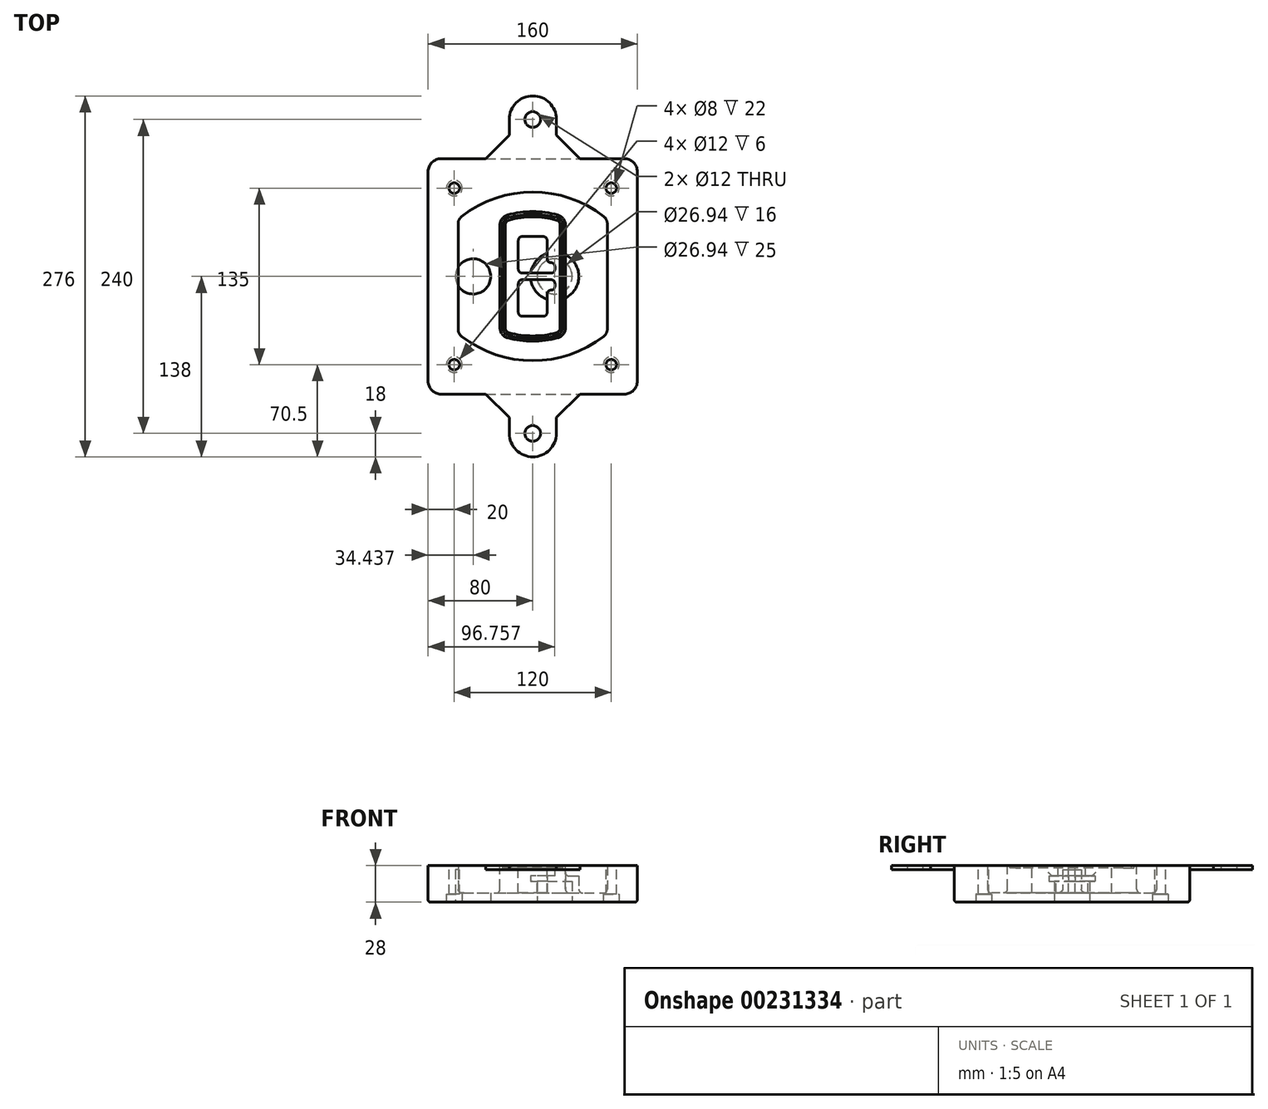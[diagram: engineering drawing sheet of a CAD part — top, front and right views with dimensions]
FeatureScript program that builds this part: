
annotation { "Feature Type Name" : "Feature", "Feature Type Description" : "" }
export const myFeature = defineFeature(function(context is Context, id is Id, definition is map)
    precondition{}
    {
        {
            var Q0;
            Q0=qCreatedBy(makeId("Top.planeOp"),FACE);
            var sketch = newSketch(context, id + "F0", { "sketchPlane" : qUnion([Q0])});
            skPoint(sketch, "E0.rect.middle", {"position": v(0, 0) * mm});
            skLineSegment(sketch, "E1.bottom", {"start": v(-70, -90) * mm, "end": v(70, -90) * mm});
            skLineSegment(sketch, "E1.top", {"start": v(-70, 90) * mm, "end": v(70, 90) * mm});
            skLineSegment(sketch, "E1.left", {"start": v(-80, -80) * mm, "end": v(-80, 80) * mm});
            skLineSegment(sketch, "E1.right", {"start": v(80, -80) * mm, "end": v(80, 80) * mm});
            skLineSegment(sketch, "E2", {"start": v(-80, 90) * mm, "end": v(80, -90) * mm, "construction": true});
            skLineSegment(sketch, "E3", {"start": v(80, 90) * mm, "end": v(-80, -90) * mm, "construction": true});
            skCircle(sketch, "E4", {"center": v(-60, 67.5) * mm, "radius": 4 * mm});
            skCircle(sketch, "E5", {"center": v(60, 67.5) * mm, "radius": 4 * mm});
            skCircle(sketch, "E6", {"center": v(60, -67.5) * mm, "radius": 4 * mm});
            skCircle(sketch, "E7", {"center": v(-60, -67.5) * mm, "radius": 4 * mm});
            skLineSegment(sketch, "E8", {"start": v(-60, 67.5) * mm, "end": v(60, 67.5) * mm, "construction": true});
            skLineSegment(sketch, "E9", {"start": v(60, 67.5) * mm, "end": v(60, -67.5) * mm, "construction": true});
            skLineSegment(sketch, "E10", {"start": v(60, -67.5) * mm, "end": v(-60, -67.5) * mm, "construction": true});
            skLineSegment(sketch, "E11", {"start": v(-60, -67.5) * mm, "end": v(-60, 67.5) * mm, "construction": true});
            skLineSegment(sketch, "E12", {"start": v(-60, 40.3) * mm, "end": v(-60, -40.3) * mm});
            skLineSegment(sketch, "E13", {"start": v(60, 40.3) * mm, "end": v(60, -40.3) * mm});
            skArc(sketch, "E14", {"start": v(56.15, 48.18) * mm, "mid": v(0, 67.5) * mm, "end": v(-56.15, 48.18) * mm});
            skArc(sketch, "E15", {"start": v(-56.15, -48.18) * mm, "mid": v(0, -67.5) * mm, "end": v(56.15, -48.18) * mm});
            skLineSegment(sketch, "E16", {"start": v(-60, 0) * mm, "end": v(60, 0) * mm, "construction": true});
            skPoint(sketch, "E17.visualSharp", {"position": v(-60, -45) * mm});
            skArc(sketch, "E17.filletArc", {"start": v(-60, -40.3) * mm, "mid": v(-58.99, -44.68) * mm, "end": v(-56.15, -48.18) * mm});
            skPoint(sketch, "E18.visualSharp", {"position": v(-60, 45) * mm});
            skArc(sketch, "E18.filletArc", {"start": v(-56.15, 48.18) * mm, "mid": v(-58.99, 44.68) * mm, "end": v(-60, 40.3) * mm});
            skPoint(sketch, "E19.visualSharp", {"position": v(60, 45) * mm});
            skArc(sketch, "E19.filletArc", {"start": v(60, 40.3) * mm, "mid": v(58.99, 44.68) * mm, "end": v(56.15, 48.18) * mm});
            skPoint(sketch, "E20.visualSharp", {"position": v(60, -45) * mm});
            skArc(sketch, "E20.filletArc", {"start": v(56.15, -48.18) * mm, "mid": v(58.99, -44.68) * mm, "end": v(60, -40.3) * mm});
            skPoint(sketch, "E21.visualSharp", {"position": v(-80, 90) * mm});
            skArc(sketch, "E21.filletArc", {"start": v(-70, 90) * mm, "mid": v(-77.07, 87.07) * mm, "end": v(-80, 80) * mm});
            skPoint(sketch, "E22.visualSharp", {"position": v(80, 90) * mm});
            skArc(sketch, "E22.filletArc", {"start": v(80, 80) * mm, "mid": v(77.07, 87.07) * mm, "end": v(70, 90) * mm});
            skPoint(sketch, "E23.visualSharp", {"position": v(80, -90) * mm});
            skArc(sketch, "E23.filletArc", {"start": v(70, -90) * mm, "mid": v(77.07, -87.07) * mm, "end": v(80, -80) * mm});
            skPoint(sketch, "E24.visualSharp", {"position": v(-80, -90) * mm});
            skArc(sketch, "E24.filletArc", {"start": v(-80, -80) * mm, "mid": v(-77.07, -87.07) * mm, "end": v(-70, -90) * mm});
            skArc(sketch, "E25.0", {"start": v(57, 40.3) * mm, "mid": v(56.3, 43.36) * mm, "end": v(54.3, 45.81) * mm});
            skLineSegment(sketch, "E25.1", {"start": v(57, 40.3) * mm, "end": v(57, -40.3) * mm});
            skArc(sketch, "E25.2", {"start": v(54.3, -45.81) * mm, "mid": v(56.3, -43.36) * mm, "end": v(57, -40.3) * mm});
            skArc(sketch, "E25.3", {"start": v(-54.3, -45.81) * mm, "mid": v(0, -64.5) * mm, "end": v(54.3, -45.81) * mm});
            skArc(sketch, "E25.4", {"start": v(-57, -40.3) * mm, "mid": v(-56.3, -43.36) * mm, "end": v(-54.3, -45.81) * mm});
            skArc(sketch, "E25.5", {"start": v(54.3, 45.81) * mm, "mid": v(0, 64.5) * mm, "end": v(-54.3, 45.81) * mm});
            skLineSegment(sketch, "E25.6", {"start": v(-57, 40.3) * mm, "end": v(-57, -40.3) * mm});
            skArc(sketch, "E25.7", {"start": v(-54.3, 45.81) * mm, "mid": v(-56.3, 43.36) * mm, "end": v(-57, 40.3) * mm});
            skArc(sketch, "E26.0", {"start": v(-58.62, 51.33) * mm, "mid": v(-62.58, 46.43) * mm, "end": v(-64, 40.3) * mm});
            skArc(sketch, "E26.1", {"start": v(58.62, 51.33) * mm, "mid": v(0, 71.5) * mm, "end": v(-58.62, 51.33) * mm});
            skArc(sketch, "E26.2", {"start": v(64, 40.3) * mm, "mid": v(62.58, 46.43) * mm, "end": v(58.62, 51.33) * mm});
            skLineSegment(sketch, "E26.3", {"start": v(64, 40.3) * mm, "end": v(64, -40.3) * mm});
            skArc(sketch, "E26.4", {"start": v(58.62, -51.33) * mm, "mid": v(62.58, -46.43) * mm, "end": v(64, -40.3) * mm});
            skLineSegment(sketch, "E26.5", {"start": v(-64, 40.3) * mm, "end": v(-64, -40.3) * mm});
            skArc(sketch, "E26.6", {"start": v(-58.62, -51.33) * mm, "mid": v(0, -71.5) * mm, "end": v(58.62, -51.33) * mm});
            skArc(sketch, "E26.7", {"start": v(-64, -40.3) * mm, "mid": v(-62.58, -46.43) * mm, "end": v(-58.62, -51.33) * mm});
            skSolve(sketch);
        }
        {
            var Q0;
            Q0=makeQuery(id+"F0.imprint","IMPRINT",FACE,{"disambiguationData":[TD([[makeQuery(id+"F0.imprint","IMPRINT",EDGE,{"derivedFrom":sQuery(id+"F0.wireOp",EDGE,"E1.bottom")}),1.0]])]});
            var Q1;
            Q1=makeQuery(id+"F0.imprint","IMPRINT",FACE,{"disambiguationData":[TD([[makeQuery(id+"F0.imprint","IMPRINT",EDGE,{"derivedFrom":sQuery(id+"F0.wireOp",EDGE,"E12")}),1.0]])]});
            var Q2;
            Q2=makeQuery(id+"F0.imprint","IMPRINT",FACE,{"disambiguationData":[TD([[makeQuery(id+"F0.imprint","IMPRINT",EDGE,{"derivedFrom":sQuery(id+"F0.wireOp",EDGE,"E25.0")}),1.0]])]});
            var Q3;
            Q3=makeQuery(id+"F0.imprint","IMPRINT",FACE,{"disambiguationData":[TD([[makeQuery(id+"F0.imprint","IMPRINT",EDGE,{"derivedFrom":sQuery(id+"F0.wireOp",EDGE,"E12")}),-1.0]])]});
            extrude(context, id + "F1", {"entities" : qUnion([Q0, Q1, Q2, Q3]), "oppositeDirection" : true, "depth" : 25 * mm});
        }
        {
            var Q0;
            Q0=makeQuery(id+"F0.imprint","IMPRINT",FACE,{"disambiguationData":[TD([[makeQuery(id+"F0.imprint","IMPRINT",EDGE,{"derivedFrom":sQuery(id+"F0.wireOp",EDGE,"E12")}),1.0]])]});
            extrude(context, id + "F2", {"entities" : qUnion([Q0]), "operationType" : NewBodyOperationType.ADD, "depth" : 3 * mm});
        }
        {
            var Q0;
            Q0=makeQuery(id+"F0.imprint","IMPRINT",FACE,{"disambiguationData":[TD([[makeQuery(id+"F0.imprint","IMPRINT",EDGE,{"derivedFrom":sQuery(id+"F0.wireOp",EDGE,"E25.0")}),1.0]])]});
            extrude(context, id + "F3", {"entities" : qUnion([Q0]), "operationType" : NewBodyOperationType.REMOVE, "oppositeDirection" : true, "depth" : 18 * mm});
        }
        {
            var Q0;
            Q0=makeQuery(id+"F2.opExtrude","CAP_FACE",FACE,{"disambiguationData":[OSD([sQuery(id+"F0.wireOp",EDGE,"E12"),sQuery(id+"F0.wireOp",EDGE,"E13"),sQuery(id+"F0.wireOp",EDGE,"E14"),sQuery(id+"F0.wireOp",EDGE,"E15"),sQuery(id+"F0.wireOp",EDGE,"E17.filletArc"),sQuery(id+"F0.wireOp",EDGE,"E18.filletArc"),sQuery(id+"F0.wireOp",EDGE,"E19.filletArc"),sQuery(id+"F0.wireOp",EDGE,"E20.filletArc"),sQuery(id+"F0.wireOp",EDGE,"E25.0"),sQuery(id+"F0.wireOp",EDGE,"E25.1"),sQuery(id+"F0.wireOp",EDGE,"E25.2"),sQuery(id+"F0.wireOp",EDGE,"E25.3"),sQuery(id+"F0.wireOp",EDGE,"E25.4"),sQuery(id+"F0.wireOp",EDGE,"E25.5"),sQuery(id+"F0.wireOp",EDGE,"E25.6"),sQuery(id+"F0.wireOp",EDGE,"E25.7")])],"isStart":false});
            var sketch = newSketch(context, id + "F4", { "sketchPlane" : qUnion([Q0])});
            skArc(sketch, "E27.0", {"start": v(-19.08, -46.97) * mm, "mid": v(0, -49.5) * mm, "end": v(19.08, -46.97) * mm});
            skArc(sketch, "E28.0", {"start": v(19.08, 46.97) * mm, "mid": v(0, 49.5) * mm, "end": v(-19.08, 46.97) * mm});
            skLineSegment(sketch, "E29", {"start": v(-25, 39.25) * mm, "end": v(-25, -39.25) * mm});
            skLineSegment(sketch, "E30", {"start": v(25, 39.25) * mm, "end": v(25, -39.25) * mm});
            skLineSegment(sketch, "E31", {"start": v(-25, 45.1) * mm, "end": v(25, 45.1) * mm, "construction": true});
            skLineSegment(sketch, "E32", {"start": v(-25, -45.1) * mm, "end": v(25, -45.1) * mm, "construction": true});
            skPoint(sketch, "E33.visualSharp", {"position": v(-25, 45.1) * mm});
            skArc(sketch, "E33.filletArc", {"start": v(-19.08, 46.97) * mm, "mid": v(-23.35, 44.11) * mm, "end": v(-25, 39.25) * mm});
            skPoint(sketch, "E34.visualSharp", {"position": v(25, 45.1) * mm});
            skArc(sketch, "E34.filletArc", {"start": v(25, 39.25) * mm, "mid": v(23.35, 44.11) * mm, "end": v(19.08, 46.97) * mm});
            skPoint(sketch, "E35.visualSharp", {"position": v(25, -45.1) * mm});
            skArc(sketch, "E35.filletArc", {"start": v(19.08, -46.97) * mm, "mid": v(23.35, -44.11) * mm, "end": v(25, -39.25) * mm});
            skPoint(sketch, "E36.visualSharp", {"position": v(-25, -45.1) * mm});
            skArc(sketch, "E36.filletArc", {"start": v(-25, -39.25) * mm, "mid": v(-23.35, -44.11) * mm, "end": v(-19.08, -46.97) * mm});
            skArc(sketch, "E37.0", {"start": v(54.3, 45.81) * mm, "mid": v(0, 64.5) * mm, "end": v(-54.3, 45.81) * mm});
            skArc(sketch, "E37.1", {"start": v(-54.3, 45.81) * mm, "mid": v(-56.3, 43.36) * mm, "end": v(-57, 40.3) * mm});
            skLineSegment(sketch, "E37.2", {"start": v(-57, 40.3) * mm, "end": v(-57, -40.3) * mm});
            skArc(sketch, "E37.3", {"start": v(-57, -40.3) * mm, "mid": v(-56.3, -43.36) * mm, "end": v(-54.3, -45.81) * mm});
            skArc(sketch, "E37.4", {"start": v(-54.3, -45.81) * mm, "mid": v(0, -64.5) * mm, "end": v(54.3, -45.81) * mm});
            skArc(sketch, "E37.5", {"start": v(54.3, -45.81) * mm, "mid": v(56.3, -43.36) * mm, "end": v(57, -40.3) * mm});
            skLineSegment(sketch, "E37.6", {"start": v(57, 40.3) * mm, "end": v(57, -40.3) * mm});
            skArc(sketch, "E37.7", {"start": v(57, 40.3) * mm, "mid": v(56.3, 43.36) * mm, "end": v(54.3, 45.81) * mm});
            skLineSegment(sketch, "E38.0", {"start": v(23, 39.25) * mm, "end": v(23, -39.25) * mm});
            skArc(sketch, "E38.1", {"start": v(18.56, -45.04) * mm, "mid": v(21.76, -42.9) * mm, "end": v(23, -39.25) * mm});
            skArc(sketch, "E38.2", {"start": v(-18.56, -45.04) * mm, "mid": v(0, -47.5) * mm, "end": v(18.56, -45.04) * mm});
            skArc(sketch, "E38.3", {"start": v(-23, -39.25) * mm, "mid": v(-21.76, -42.9) * mm, "end": v(-18.56, -45.04) * mm});
            skLineSegment(sketch, "E38.4", {"start": v(-23, 39.25) * mm, "end": v(-23, -39.25) * mm});
            skArc(sketch, "E38.5", {"start": v(23, 39.25) * mm, "mid": v(21.76, 42.9) * mm, "end": v(18.56, 45.04) * mm});
            skArc(sketch, "E38.6", {"start": v(-18.56, 45.04) * mm, "mid": v(-21.76, 42.9) * mm, "end": v(-23, 39.25) * mm});
            skArc(sketch, "E38.7", {"start": v(18.56, 45.04) * mm, "mid": v(0, 47.5) * mm, "end": v(-18.56, 45.04) * mm});
            skArc(sketch, "E39.0", {"start": v(21, 39.25) * mm, "mid": v(20.18, 41.68) * mm, "end": v(18.04, 43.1) * mm});
            skLineSegment(sketch, "E39.1", {"start": v(21, 39.25) * mm, "end": v(21, -39.25) * mm});
            skArc(sketch, "E39.2", {"start": v(18.04, -43.1) * mm, "mid": v(20.18, -41.68) * mm, "end": v(21, -39.25) * mm});
            skArc(sketch, "E39.3", {"start": v(-18.04, -43.1) * mm, "mid": v(0, -45.5) * mm, "end": v(18.04, -43.1) * mm});
            skArc(sketch, "E39.4", {"start": v(-21, -39.25) * mm, "mid": v(-20.18, -41.68) * mm, "end": v(-18.04, -43.1) * mm});
            skArc(sketch, "E39.5", {"start": v(18.04, 43.1) * mm, "mid": v(0, 45.5) * mm, "end": v(-18.04, 43.1) * mm});
            skLineSegment(sketch, "E39.6", {"start": v(-21, 39.25) * mm, "end": v(-21, -39.25) * mm});
            skArc(sketch, "E39.7", {"start": v(-18.04, 43.1) * mm, "mid": v(-20.18, 41.68) * mm, "end": v(-21, 39.25) * mm});
            skLineSegment(sketch, "E40", {"start": v(-25, 0) * mm, "end": v(25, 0) * mm, "construction": true});
            skLineSegment(sketch, "E41", {"start": v(-11, 5.5) * mm, "end": v(-11, 27.5) * mm});
            skLineSegment(sketch, "E42", {"start": v(-8, 30.5) * mm, "end": v(8, 30.5) * mm});
            skLineSegment(sketch, "E43", {"start": v(11, 27.5) * mm, "end": v(11, 13.5) * mm});
            skLineSegment(sketch, "E44", {"start": v(14, 10.5) * mm, "end": v(14, 10.5) * mm});
            skLineSegment(sketch, "E45", {"start": v(17, 7.5) * mm, "end": v(17, 5.5) * mm});
            skLineSegment(sketch, "E46", {"start": v(14, 2.5) * mm, "end": v(-8, 2.5) * mm});
            skPoint(sketch, "E47.visualSharp", {"position": v(-11, 30.5) * mm});
            skArc(sketch, "E47.filletArc", {"start": v(-8, 30.5) * mm, "mid": v(-10.12, 29.62) * mm, "end": v(-11, 27.5) * mm});
            skPoint(sketch, "E48.visualSharp", {"position": v(11, 30.5) * mm});
            skArc(sketch, "E48.filletArc", {"start": v(11, 27.5) * mm, "mid": v(10.12, 29.62) * mm, "end": v(8, 30.5) * mm});
            skPoint(sketch, "E49.visualSharp", {"position": v(11, 10.5) * mm});
            skArc(sketch, "E49.filletArc", {"start": v(11, 13.5) * mm, "mid": v(11.88, 11.38) * mm, "end": v(14, 10.5) * mm});
            skPoint(sketch, "E50.visualSharp", {"position": v(17, 10.5) * mm});
            skArc(sketch, "E50.filletArc", {"start": v(17, 7.5) * mm, "mid": v(16.12, 9.62) * mm, "end": v(14, 10.5) * mm});
            skPoint(sketch, "E51.visualSharp", {"position": v(17, 2.5) * mm});
            skArc(sketch, "E51.filletArc", {"start": v(14, 2.5) * mm, "mid": v(16.12, 3.38) * mm, "end": v(17, 5.5) * mm});
            skPoint(sketch, "E52.visualSharp", {"position": v(-11, 2.5) * mm});
            skArc(sketch, "E52.filletArc", {"start": v(-11, 5.5) * mm, "mid": v(-10.12, 3.38) * mm, "end": v(-8, 2.5) * mm});
            skLineSegment(sketch, "E53.0.MirrorCS", {"start": v(14, -2.5) * mm, "end": v(-8, -2.5) * mm});
            skArc(sketch, "E54.0.MirrorCS", {"start": v(-11, -5.5) * mm, "mid": v(-10.12, -3.38) * mm, "end": v(-8, -2.5) * mm});
            skLineSegment(sketch, "E55.0.MirrorCS", {"start": v(-11, -5.5) * mm, "end": v(-11, -27.5) * mm});
            skArc(sketch, "E56.0.MirrorCS", {"start": v(-8, -30.5) * mm, "mid": v(-10.12, -29.62) * mm, "end": v(-11, -27.5) * mm});
            skLineSegment(sketch, "E57.0.MirrorCS", {"start": v(-8, -30.5) * mm, "end": v(8, -30.5) * mm});
            skArc(sketch, "E58.0.MirrorCS", {"start": v(11, -27.5) * mm, "mid": v(10.12, -29.62) * mm, "end": v(8, -30.5) * mm});
            skLineSegment(sketch, "E59.0.MirrorCS", {"start": v(11, -27.5) * mm, "end": v(11, -13.5) * mm});
            skArc(sketch, "E60.0.MirrorCS", {"start": v(11, -13.5) * mm, "mid": v(11.88, -11.38) * mm, "end": v(14, -10.5) * mm});
            skArc(sketch, "E61.0.MirrorCS", {"start": v(17, -7.5) * mm, "mid": v(16.12, -9.62) * mm, "end": v(14, -10.5) * mm});
            skLineSegment(sketch, "E62.0.MirrorCS", {"start": v(17, -7.5) * mm, "end": v(17, -5.5) * mm});
            skArc(sketch, "E63.0.MirrorCS", {"start": v(14, -2.5) * mm, "mid": v(16.12, -3.38) * mm, "end": v(17, -5.5) * mm});
            skSolve(sketch);
        }
        {
            var Q0;
            Q0=makeQuery(id+"F4.imprint","IMPRINT",FACE,{"disambiguationData":[TD([[makeQuery(id+"F4.imprint","IMPRINT",EDGE,{"derivedFrom":sQuery(id+"F4.wireOp",EDGE,"E27.0")}),1.0]])]});
            var Q1;
            Q1=makeQuery(id+"F4.imprint","IMPRINT",FACE,{"disambiguationData":[TD([[makeQuery(id+"F4.imprint","IMPRINT",EDGE,{"derivedFrom":sQuery(id+"F4.wireOp",EDGE,"E38.0")}),-1.0]])]});
            var Q2;
            Q2=makeQuery(id+"F4.imprint","IMPRINT",FACE,{"disambiguationData":[TD([[makeQuery(id+"F4.imprint","IMPRINT",EDGE,{"derivedFrom":sQuery(id+"F4.wireOp",EDGE,"E39.0")}),1.0]])]});
            extrude(context, id + "F5", {"entities" : qUnion([Q0, Q1, Q2]), "operationType" : NewBodyOperationType.ADD, "endBound" : BoundingType.UP_TO_NEXT, "oppositeDirection" : true, "depth" : 25 * mm});
        }
        {
            var Q0;
            Q0=makeQuery(id+"F4.imprint","IMPRINT",FACE,{"disambiguationData":[TD([[makeQuery(id+"F4.imprint","IMPRINT",EDGE,{"derivedFrom":sQuery(id+"F4.wireOp",EDGE,"E38.0")}),-1.0]])]});
            extrude(context, id + "F6", {"entities" : qUnion([Q0]), "operationType" : NewBodyOperationType.REMOVE, "oppositeDirection" : true, "depth" : 2 * mm});
        }
        {
            var Q0;
            Q0=makeQuery(id+"F1.opExtrude","CAP_FACE",FACE,{"disambiguationData":[OSD([sQuery(id+"F0.wireOp",EDGE,"E1.bottom"),sQuery(id+"F0.wireOp",EDGE,"E1.top"),sQuery(id+"F0.wireOp",EDGE,"E1.left"),sQuery(id+"F0.wireOp",EDGE,"E1.right"),sQuery(id+"F0.wireOp",EDGE,"E4"),sQuery(id+"F0.wireOp",EDGE,"E5"),sQuery(id+"F0.wireOp",EDGE,"E6"),sQuery(id+"F0.wireOp",EDGE,"E7"),sQuery(id+"F0.wireOp",EDGE,"E21.filletArc"),sQuery(id+"F0.wireOp",EDGE,"E22.filletArc"),sQuery(id+"F0.wireOp",EDGE,"E23.filletArc"),sQuery(id+"F0.wireOp",EDGE,"E24.filletArc")])],"isStart":false});
            var sketch = newSketch(context, id + "F7", { "sketchPlane" : qUnion([Q0])});
            skCircle(sketch, "E64", {"center": v(16.76, 0) * mm, "radius": 13.47 * mm});
            skCircle(sketch, "E65", {"center": v(-45.56, 0) * mm, "radius": 13.47 * mm});
            skLineSegment(sketch, "E66", {"start": v(80, 0) * mm, "end": v(-80, 0) * mm});
            skCircle(sketch, "E67", {"center": v(16.76, 0) * mm, "radius": 18.47 * mm});
            skCircle(sketch, "E68", {"center": v(60, -67.5) * mm, "radius": 6 * mm});
            skCircle(sketch, "E69", {"center": v(-60, -67.5) * mm, "radius": 6 * mm});
            skCircle(sketch, "E70", {"center": v(-60, 67.5) * mm, "radius": 6 * mm});
            skCircle(sketch, "E71", {"center": v(60, 67.5) * mm, "radius": 6 * mm});
            skSolve(sketch);
        }
        {
            var Q0;
            {var subQ1=sQuery(id+"F7.wireOp",EDGE,"E66");var subQ4=sQuery(id+"F7.wireOp",EDGE,"E64");var subQ6=makeQuery(id+"F7.imprint","INTERSECT",VERTEX,{"disambiguationData":[OD(0.0)],"derivedFrom":[subQ4,subQ1]});Q0=makeQuery(id+"F7.imprint","IMPRINT",FACE,{"disambiguationData":[TD([[makeQuery(id+"F7.imprint","IMPRINT",EDGE,{"disambiguationData":[TD([[subQ6,-1.0]])],"derivedFrom":subQ4}),-1.0]])]});}
            var Q1;
            {var subQ0=sQuery(id+"F7.wireOp",EDGE,"E66");var subQ1=sQuery(id+"F7.wireOp",EDGE,"E64");var subQ3=makeQuery(id+"F7.imprint","INTERSECT",VERTEX,{"disambiguationData":[OD(0.0)],"derivedFrom":[subQ1,subQ0]});Q1=makeQuery(id+"F7.imprint","IMPRINT",FACE,{"disambiguationData":[TD([[makeQuery(id+"F7.imprint","IMPRINT",EDGE,{"disambiguationData":[TD([[subQ3,-1.0]])],"derivedFrom":subQ1}),1.0]])]});}
            var Q2;
            {var subQ0=sQuery(id+"F7.wireOp",EDGE,"E66");var subQ1=sQuery(id+"F7.wireOp",EDGE,"E64");var subQ3=makeQuery(id+"F7.imprint","INTERSECT",VERTEX,{"disambiguationData":[OD(0.0)],"derivedFrom":[subQ1,subQ0]});Q2=makeQuery(id+"F7.imprint","IMPRINT",FACE,{"disambiguationData":[TD([[makeQuery(id+"F7.imprint","IMPRINT",EDGE,{"disambiguationData":[TD([[subQ3,1.0]])],"derivedFrom":subQ1}),1.0]])]});}
            var Q3;
            {var subQ1=sQuery(id+"F7.wireOp",EDGE,"E66");var subQ4=sQuery(id+"F7.wireOp",EDGE,"E64");var subQ6=makeQuery(id+"F7.imprint","INTERSECT",VERTEX,{"disambiguationData":[OD(0.0)],"derivedFrom":[subQ4,subQ1]});Q3=makeQuery(id+"F7.imprint","IMPRINT",FACE,{"disambiguationData":[TD([[makeQuery(id+"F7.imprint","IMPRINT",EDGE,{"disambiguationData":[TD([[subQ6,1.0]])],"derivedFrom":subQ4}),-1.0]])]});}
            extrude(context, id + "F8", {"entities" : qUnion([Q0, Q1, Q2, Q3]), "operationType" : NewBodyOperationType.ADD, "oppositeDirection" : true, "depth" : 20 * mm});
        }
        {
            var Q0;
            {var subQ0=sQuery(id+"F7.wireOp",EDGE,"E66");var subQ1=sQuery(id+"F7.wireOp",EDGE,"E64");var subQ3=makeQuery(id+"F7.imprint","INTERSECT",VERTEX,{"disambiguationData":[OD(0.0)],"derivedFrom":[subQ1,subQ0]});Q0=makeQuery(id+"F7.imprint","IMPRINT",FACE,{"disambiguationData":[TD([[makeQuery(id+"F7.imprint","IMPRINT",EDGE,{"disambiguationData":[TD([[subQ3,-1.0]])],"derivedFrom":subQ1}),1.0]])]});}
            var Q1;
            {var subQ0=sQuery(id+"F7.wireOp",EDGE,"E66");var subQ1=sQuery(id+"F7.wireOp",EDGE,"E64");var subQ3=makeQuery(id+"F7.imprint","INTERSECT",VERTEX,{"disambiguationData":[OD(0.0)],"derivedFrom":[subQ1,subQ0]});Q1=makeQuery(id+"F7.imprint","IMPRINT",FACE,{"disambiguationData":[TD([[makeQuery(id+"F7.imprint","IMPRINT",EDGE,{"disambiguationData":[TD([[subQ3,1.0]])],"derivedFrom":subQ1}),1.0]])]});}
            extrude(context, id + "F9", {"entities" : qUnion([Q0, Q1]), "operationType" : NewBodyOperationType.REMOVE, "oppositeDirection" : true, "depth" : 16 * mm});
        }
        {
            var Q0;
            {var subQ0=sQuery(id+"F7.wireOp",EDGE,"E66");var subQ1=sQuery(id+"F7.wireOp",EDGE,"E65");var subQ3=makeQuery(id+"F7.imprint","INTERSECT",VERTEX,{"disambiguationData":[OD(0.0)],"derivedFrom":[subQ1,subQ0]});Q0=makeQuery(id+"F7.imprint","IMPRINT",FACE,{"disambiguationData":[TD([[makeQuery(id+"F7.imprint","IMPRINT",EDGE,{"disambiguationData":[TD([[subQ3,-1.0]])],"derivedFrom":subQ1}),1.0]])]});}
            var Q1;
            {var subQ0=sQuery(id+"F7.wireOp",EDGE,"E66");var subQ1=sQuery(id+"F7.wireOp",EDGE,"E65");var subQ3=makeQuery(id+"F7.imprint","INTERSECT",VERTEX,{"disambiguationData":[OD(0.0)],"derivedFrom":[subQ1,subQ0]});Q1=makeQuery(id+"F7.imprint","IMPRINT",FACE,{"disambiguationData":[TD([[makeQuery(id+"F7.imprint","IMPRINT",EDGE,{"disambiguationData":[TD([[subQ3,1.0]])],"derivedFrom":subQ1}),1.0]])]});}
            extrude(context, id + "F10", {"entities" : qUnion([Q0, Q1]), "operationType" : NewBodyOperationType.REMOVE, "oppositeDirection" : true, "depth" : 25 * mm});
        }
        {
            var Q0;
            Q0=makeQuery(id+"F7.imprint","IMPRINT",FACE,{"disambiguationData":[TD([[makeQuery(id+"F7.imprint","IMPRINT",EDGE,{"derivedFrom":sQuery(id+"F7.wireOp",EDGE,"E68")}),1.0]])]});
            var Q1;
            Q1=makeQuery(id+"F7.imprint","IMPRINT",FACE,{"disambiguationData":[TD([[makeQuery(id+"F7.imprint","IMPRINT",EDGE,{"derivedFrom":makeQuery(id+"F1.opExtrude","CAP_EDGE",EDGE,{"disambiguationData":[OSD([sQuery(id+"F0.wireOp",EDGE,"E5")])],"isStart":false})}),-1.0]])]});
            var Q2;
            Q2=makeQuery(id+"F7.imprint","IMPRINT",FACE,{"disambiguationData":[TD([[makeQuery(id+"F7.imprint","IMPRINT",EDGE,{"derivedFrom":sQuery(id+"F7.wireOp",EDGE,"E69")}),1.0]])]});
            var Q3;
            Q3=makeQuery(id+"F7.imprint","IMPRINT",FACE,{"disambiguationData":[TD([[makeQuery(id+"F7.imprint","IMPRINT",EDGE,{"derivedFrom":makeQuery(id+"F1.opExtrude","CAP_EDGE",EDGE,{"disambiguationData":[OSD([sQuery(id+"F0.wireOp",EDGE,"E4")])],"isStart":false})}),-1.0]])]});
            var Q4;
            Q4=makeQuery(id+"F7.imprint","IMPRINT",FACE,{"disambiguationData":[TD([[makeQuery(id+"F7.imprint","IMPRINT",EDGE,{"derivedFrom":sQuery(id+"F7.wireOp",EDGE,"E70")}),1.0]])]});
            var Q5;
            Q5=makeQuery(id+"F7.imprint","IMPRINT",FACE,{"disambiguationData":[TD([[makeQuery(id+"F7.imprint","IMPRINT",EDGE,{"derivedFrom":makeQuery(id+"F1.opExtrude","CAP_EDGE",EDGE,{"disambiguationData":[OSD([sQuery(id+"F0.wireOp",EDGE,"E7")])],"isStart":false})}),-1.0]])]});
            var Q6;
            Q6=makeQuery(id+"F7.imprint","IMPRINT",FACE,{"disambiguationData":[TD([[makeQuery(id+"F7.imprint","IMPRINT",EDGE,{"derivedFrom":sQuery(id+"F7.wireOp",EDGE,"E71")}),1.0]])]});
            var Q7;
            Q7=makeQuery(id+"F7.imprint","IMPRINT",FACE,{"disambiguationData":[TD([[makeQuery(id+"F7.imprint","IMPRINT",EDGE,{"derivedFrom":makeQuery(id+"F1.opExtrude","CAP_EDGE",EDGE,{"disambiguationData":[OSD([sQuery(id+"F0.wireOp",EDGE,"E6")])],"isStart":false})}),-1.0]])]});
            extrude(context, id + "F11", {"entities" : qUnion([Q0, Q1, Q2, Q3, Q4, Q5, Q6, Q7]), "operationType" : NewBodyOperationType.REMOVE, "oppositeDirection" : true, "depth" : 6 * mm});
        }
        {
            var Q0;
            Q0=makeQuery(id+"F9.boolean.opBoolean","COPY",FACE,{"derivedFrom":makeQuery(id+"F9.opExtrude","CAP_FACE",FACE,{"disambiguationData":[OSD([sQuery(id+"F7.wireOp",EDGE,"E64")])],"isStart":false})});
            var sketch = newSketch(context, id + "F12", { "sketchPlane" : qUnion([Q0])});
            skArc(sketch, "E72.0", {"start": v(11, 17.55) * mm, "mid": v(2.57, 11.82) * mm, "end": v(-1.54, 2.5) * mm});
            skArc(sketch, "E72.1", {"start": v(-1.54, -2.5) * mm, "mid": v(2.57, -11.82) * mm, "end": v(11, -17.55) * mm});
            skLineSegment(sketch, "E73", {"start": v(-1.54, -2.5) * mm, "end": v(14, -2.5) * mm});
            skLineSegment(sketch, "E74.0", {"start": v(14, 2.5) * mm, "end": v(-1.54, 2.5) * mm});
            skArc(sketch, "E74.1", {"start": v(14, 2.5) * mm, "mid": v(16.12, 3.38) * mm, "end": v(17, 5.5) * mm});
            skLineSegment(sketch, "E74.2", {"start": v(17, 7.5) * mm, "end": v(17, 5.5) * mm});
            skArc(sketch, "E74.3", {"start": v(17, 7.5) * mm, "mid": v(16.12, 9.62) * mm, "end": v(14, 10.5) * mm});
            skArc(sketch, "E74.4", {"start": v(11, 13.5) * mm, "mid": v(11.88, 11.38) * mm, "end": v(14, 10.5) * mm});
            skLineSegment(sketch, "E74.5", {"start": v(11, 17.55) * mm, "end": v(11, 13.5) * mm});
            skLineSegment(sketch, "E74.7", {"start": v(14, -2.5) * mm, "end": v(-1.54, -2.5) * mm});
            skArc(sketch, "E74.8", {"start": v(14, -2.5) * mm, "mid": v(16.12, -3.38) * mm, "end": v(17, -5.5) * mm});
            skLineSegment(sketch, "E74.9", {"start": v(17, -7.5) * mm, "end": v(17, -5.5) * mm});
            skArc(sketch, "E74.10", {"start": v(17, -7.5) * mm, "mid": v(16.12, -9.62) * mm, "end": v(14, -10.5) * mm});
            skArc(sketch, "E74.11", {"start": v(11, -13.5) * mm, "mid": v(11.88, -11.38) * mm, "end": v(14, -10.5) * mm});
            skLineSegment(sketch, "E74.12", {"start": v(11, -17.55) * mm, "end": v(11, -13.5) * mm});
            skPoint(sketch, "E75.orphan", {"position": v(11, -27.5) * mm});
            skPoint(sketch, "E76.orphan", {"position": v(-8, -2.5) * mm});
            skPoint(sketch, "E77.orphan", {"position": v(-8, 2.5) * mm});
            skPoint(sketch, "E78.orphan", {"position": v(11, 27.5) * mm});
            skSolve(sketch);
        }
        {
            var Q0;
            {var subQ7=sQuery(id+"F12.wireOp",EDGE,"E72.0");var subQ14=sQuery(id+"F12.wireOp",EDGE,"E72.1");var subQ16=sQuery(id+"F12.wireOp",EDGE,"E74.1");var subQ18=sQuery(id+"F12.wireOp",EDGE,"E74.8");Q0=qUnion([makeQuery(id+"F12.imprint","IMPRINT",FACE,{"disambiguationData":[TD([[makeQuery(id+"F12.imprint","IMPRINT",EDGE,{"derivedFrom":subQ7}),1.0]])]}),makeQuery(id+"F12.imprint","IMPRINT",FACE,{"disambiguationData":[TD([[makeQuery(id+"F12.imprint","IMPRINT",EDGE,{"derivedFrom":subQ14}),1.0]])]}),makeQuery(id+"F12.imprint","IMPRINT",FACE,{"disambiguationData":[TD([[makeQuery(id+"F12.imprint","IMPRINT",EDGE,{"derivedFrom":subQ16}),1.0]])]}),makeQuery(id+"F12.imprint","IMPRINT",FACE,{"disambiguationData":[TD([[makeQuery(id+"F12.imprint","IMPRINT",EDGE,{"derivedFrom":subQ18}),-1.0]])]})]);}
            var Q1;
            Q1=makeQuery(id+"F5.boolean.opBoolean","SPLIT",FACE,{"disambiguationData":[TD([makeQuery(id+"F5.opExtrude","SWEPT_FACE",FACE,{"disambiguationData":[OSD([sQuery(id+"F4.wireOp",EDGE,"E41")])]})])],"derivedFrom":makeQuery(id+"F3.boolean.opBoolean","COPY",FACE,{"derivedFrom":makeQuery(id+"F3.opExtrude","CAP_FACE",FACE,{"disambiguationData":[OSD([sQuery(id+"F0.wireOp",EDGE,"E25.0"),sQuery(id+"F0.wireOp",EDGE,"E25.1"),sQuery(id+"F0.wireOp",EDGE,"E25.2"),sQuery(id+"F0.wireOp",EDGE,"E25.3"),sQuery(id+"F0.wireOp",EDGE,"E25.4"),sQuery(id+"F0.wireOp",EDGE,"E25.5"),sQuery(id+"F0.wireOp",EDGE,"E25.6"),sQuery(id+"F0.wireOp",EDGE,"E25.7")])],"isStart":false})})});
            extrude(context, id + "F13", {"entities" : qUnion([Q0]), "operationType" : NewBodyOperationType.REMOVE, "endBound" : BoundingType.UP_TO_SURFACE, "endBoundEntityFace" : qUnion([Q1]), "depth" : 25 * mm});
        }
        {
            var Q0;
            Q0=makeQuery(id+"F3.boolean.opBoolean","COPY",EDGE,{"derivedFrom":makeQuery(id+"F3.opExtrude","CAP_EDGE",EDGE,{"disambiguationData":[OSD([sQuery(id+"F0.wireOp",EDGE,"E25.6")])],"isStart":false})});
            var Q1;
            Q1=makeQuery(id+"F8.boolean.opBoolean","INTERSECT",EDGE,{"derivedFrom":[makeQuery(id+"F5.opExtrude","SWEPT_FACE",FACE,{"disambiguationData":[OSD([sQuery(id+"F4.wireOp",EDGE,"E30")])]}),makeQuery(id+"F8.opExtrude","CAP_FACE",FACE,{"disambiguationData":[OSD([sQuery(id+"F7.wireOp",EDGE,"E67")])],"isStart":false})]});
            var Q2;
            Q2=makeQuery(id+"F8.boolean.opBoolean","INTERSECT",EDGE,{"disambiguationData":[OD(1.0)],"derivedFrom":[makeQuery(id+"F5.opExtrude","SWEPT_FACE",FACE,{"disambiguationData":[OSD([sQuery(id+"F4.wireOp",EDGE,"E30")])]}),makeQuery(id+"F8.opExtrude","SWEPT_FACE",FACE,{"disambiguationData":[OSD([sQuery(id+"F7.wireOp",EDGE,"E67")])]})]});
            var Q3;
            {var subQ0=sQuery(id+"F4.wireOp",EDGE,"E30");Q3=makeQuery(id+"F8.boolean.opBoolean","SPLIT",EDGE,{"disambiguationData":[TD([makeQuery(id+"F5.opExtrude","SWEPT_FACE",FACE,{"disambiguationData":[OSD([sQuery(id+"F4.wireOp",EDGE,"E35.filletArc")])]})])],"derivedFrom":makeQuery(id+"F5.opExtrude","CAP_EDGE",EDGE,{"disambiguationData":[OSD([subQ0])],"isStart":false})});}
            var Q4;
            {var subQ0=sQuery(id+"F0.wireOp",EDGE,"E25.7");var subQ1=sQuery(id+"F0.wireOp",EDGE,"E25.1");var subQ2=sQuery(id+"F0.wireOp",EDGE,"E25.6");var subQ3=sQuery(id+"F0.wireOp",EDGE,"E25.5");var subQ4=sQuery(id+"F0.wireOp",EDGE,"E25.4");var subQ5=sQuery(id+"F0.wireOp",EDGE,"E25.0");var subQ6=sQuery(id+"F0.wireOp",EDGE,"E25.2");var subQ7=sQuery(id+"F0.wireOp",EDGE,"E25.3");Q4=makeQuery(id+"F8.boolean.opBoolean","INTERSECT",EDGE,{"derivedFrom":[makeQuery(id+"F5.boolean.opBoolean","SPLIT",FACE,{"disambiguationData":[TD([makeQuery(id+"F2.opExtrude","SWEPT_FACE",FACE,{"disambiguationData":[OSD([subQ5])]})])],"derivedFrom":makeQuery(id+"F3.boolean.opBoolean","COPY",FACE,{"derivedFrom":makeQuery(id+"F3.opExtrude","CAP_FACE",FACE,{"disambiguationData":[OSD([subQ5,subQ1,subQ6,subQ7,subQ4,subQ3,subQ2,subQ0])],"isStart":false})})}),makeQuery(id+"F8.opExtrude","SWEPT_FACE",FACE,{"disambiguationData":[OSD([sQuery(id+"F7.wireOp",EDGE,"E67")])]})]});}
            var Q5;
            Q5=makeQuery(id+"F8.boolean.opBoolean","INTERSECT",EDGE,{"disambiguationData":[OD(0.0)],"derivedFrom":[makeQuery(id+"F5.opExtrude","SWEPT_FACE",FACE,{"disambiguationData":[OSD([sQuery(id+"F4.wireOp",EDGE,"E30")])]}),makeQuery(id+"F8.opExtrude","SWEPT_FACE",FACE,{"disambiguationData":[OSD([sQuery(id+"F7.wireOp",EDGE,"E67")])]})]});
            fillet(context, id + "F14", {"entities" : qUnion([Q0, Q1, Q2, Q3, Q4, Q5]), "radius" : 3 * mm, "tangentPropagation" : true, "allowEdgeOverflow" : false});
        }
        {
            var Q0;
            Q0=makeQuery(id+"F1.opExtrude","CAP_EDGE",EDGE,{"disambiguationData":[OSD([sQuery(id+"F0.wireOp",EDGE,"E1.bottom")])],"isStart":false});
            fillet(context, id + "F15", {"entities" : qUnion([Q0]), "radius" : 2 * mm, "tangentPropagation" : true, "allowEdgeOverflow" : false});
        }
        {
            var Q0;
            {var subQ0=sQuery(id+"F0.wireOp",EDGE,"E22.filletArc");var subQ1=sQuery(id+"F0.wireOp",EDGE,"E7");var subQ2=sQuery(id+"F0.wireOp",EDGE,"E6");var subQ3=sQuery(id+"F0.wireOp",EDGE,"E5");var subQ4=sQuery(id+"F0.wireOp",EDGE,"E4");var subQ5=sQuery(id+"F0.wireOp",EDGE,"E1.bottom");var subQ6=sQuery(id+"F0.wireOp",EDGE,"E21.filletArc");var subQ7=sQuery(id+"F0.wireOp",EDGE,"E1.top");var subQ8=sQuery(id+"F0.wireOp",EDGE,"E1.left");var subQ9=sQuery(id+"F0.wireOp",EDGE,"E1.right");var subQ10=sQuery(id+"F0.wireOp",EDGE,"E23.filletArc");var subQ11=sQuery(id+"F0.wireOp",EDGE,"E24.filletArc");Q0=makeQuery(id+"F2.boolean.opBoolean","SPLIT",FACE,{"disambiguationData":[TD([makeQuery(id+"F1.opExtrude","SWEPT_FACE",FACE,{"disambiguationData":[OSD([subQ5])]})])],"derivedFrom":makeQuery(id+"F1.opExtrude","CAP_FACE",FACE,{"disambiguationData":[OSD([subQ5,subQ7,subQ8,subQ9,subQ4,subQ3,subQ2,subQ1,subQ6,subQ0,subQ10,subQ11])],"isStart":true})});}
            var sketch = newSketch(context, id + "F16", { "sketchPlane" : qUnion([Q0])});
            skLineSegment(sketch, "E79.0", {"start": v(-70, 90) * mm, "end": v(70, 90) * mm});
            skArc(sketch, "E79.1", {"start": v(80, 80) * mm, "mid": v(77.07, 87.07) * mm, "end": v(70, 90) * mm});
            skArc(sketch, "E79.2", {"start": v(-70, 90) * mm, "mid": v(-77.07, 87.07) * mm, "end": v(-80, 80) * mm});
            skLineSegment(sketch, "E79.3", {"start": v(-80, -80) * mm, "end": v(-80, 80) * mm});
            skCircle(sketch, "E79.4", {"center": v(-60, 67.5) * mm, "radius": 4 * mm});
            skCircle(sketch, "E79.5", {"center": v(-60, -67.5) * mm, "radius": 4 * mm});
            skArc(sketch, "E79.6", {"start": v(-80, -80) * mm, "mid": v(-77.07, -87.07) * mm, "end": v(-70, -90) * mm});
            skLineSegment(sketch, "E79.7", {"start": v(-70, -90) * mm, "end": v(70, -90) * mm});
            skCircle(sketch, "E79.8", {"center": v(60, -67.5) * mm, "radius": 4 * mm});
            skArc(sketch, "E79.9", {"start": v(70, -90) * mm, "mid": v(77.07, -87.07) * mm, "end": v(80, -80) * mm});
            skLineSegment(sketch, "E79.10", {"start": v(80, -80) * mm, "end": v(80, 80) * mm});
            skCircle(sketch, "E79.11", {"center": v(60, 67.5) * mm, "radius": 4 * mm});
            skArc(sketch, "E79.12", {"start": v(56.15, 48.18) * mm, "mid": v(0, 67.5) * mm, "end": v(-56.15, 48.18) * mm});
            skArc(sketch, "E79.13", {"start": v(60, 40.3) * mm, "mid": v(58.99, 44.68) * mm, "end": v(56.15, 48.18) * mm});
            skLineSegment(sketch, "E79.14", {"start": v(60, 40.3) * mm, "end": v(60, -40.3) * mm});
            skArc(sketch, "E79.15", {"start": v(-56.15, 48.18) * mm, "mid": v(-58.99, 44.68) * mm, "end": v(-60, 40.3) * mm});
            skLineSegment(sketch, "E79.16", {"start": v(-60, 40.3) * mm, "end": v(-60, -40.3) * mm});
            skArc(sketch, "E79.17", {"start": v(-60, -40.3) * mm, "mid": v(-58.99, -44.68) * mm, "end": v(-56.15, -48.18) * mm});
            skArc(sketch, "E79.18", {"start": v(-56.15, -48.18) * mm, "mid": v(0, -67.5) * mm, "end": v(56.15, -48.18) * mm});
            skArc(sketch, "E79.19", {"start": v(56.15, -48.18) * mm, "mid": v(58.99, -44.68) * mm, "end": v(60, -40.3) * mm});
            skLineSegment(sketch, "E80", {"start": v(-80, 0) * mm, "end": v(80, 0) * mm, "construction": true});
            skLineSegment(sketch, "E81", {"start": v(0, 90) * mm, "end": v(0, 120) * mm});
            skLineSegment(sketch, "E82", {"start": v(-35.89, 90) * mm, "end": v(-17.89, 108) * mm});
            skLineSegment(sketch, "E83", {"start": v(-17.89, 108) * mm, "end": v(-17.89, 120) * mm});
            skLineSegment(sketch, "E84", {"start": v(36.11, 90) * mm, "end": v(18.11, 108) * mm});
            skLineSegment(sketch, "E85", {"start": v(18.11, 108) * mm, "end": v(18.11, 120) * mm});
            skCircle(sketch, "E86", {"center": v(0, 120) * mm, "radius": 6 * mm});
            skArc(sketch, "E87", {"start": v(18.11, 120) * mm, "mid": v(0.11, 138) * mm, "end": v(-17.89, 120) * mm});
            skArc(sketch, "E88.MirrorCS", {"start": v(18.11, -120) * mm, "mid": v(0.11, -138) * mm, "end": v(-17.89, -120) * mm});
            skCircle(sketch, "E89.MirrorC", {"center": v(0, -120) * mm, "radius": 6 * mm});
            skLineSegment(sketch, "E90.MirrorCS", {"start": v(18.11, -108) * mm, "end": v(18.11, -120) * mm});
            skLineSegment(sketch, "E91.MirrorCS", {"start": v(36.11, -90) * mm, "end": v(18.11, -108) * mm});
            skLineSegment(sketch, "E92.MirrorCS", {"start": v(-17.89, -108) * mm, "end": v(-17.89, -120) * mm});
            skLineSegment(sketch, "E93.MirrorCS", {"start": v(-35.89, -90) * mm, "end": v(-17.89, -108) * mm});
            skSolve(sketch);
        }
        {
            var Q0;
            Q0 = qSketchRegion(id + "F16", true);
            var Q1;
            Q1=makeQuery(id+"F2.opExtrude","CAP_FACE",FACE,{"disambiguationData":[OSD([sQuery(id+"F0.wireOp",EDGE,"E12"),sQuery(id+"F0.wireOp",EDGE,"E13"),sQuery(id+"F0.wireOp",EDGE,"E14"),sQuery(id+"F0.wireOp",EDGE,"E15"),sQuery(id+"F0.wireOp",EDGE,"E17.filletArc"),sQuery(id+"F0.wireOp",EDGE,"E18.filletArc"),sQuery(id+"F0.wireOp",EDGE,"E19.filletArc"),sQuery(id+"F0.wireOp",EDGE,"E20.filletArc"),sQuery(id+"F0.wireOp",EDGE,"E25.0"),sQuery(id+"F0.wireOp",EDGE,"E25.1"),sQuery(id+"F0.wireOp",EDGE,"E25.2"),sQuery(id+"F0.wireOp",EDGE,"E25.3"),sQuery(id+"F0.wireOp",EDGE,"E25.4"),sQuery(id+"F0.wireOp",EDGE,"E25.5"),sQuery(id+"F0.wireOp",EDGE,"E25.6"),sQuery(id+"F0.wireOp",EDGE,"E25.7")])],"isStart":false});
            extrude(context, id + "F17", {"entities" : qUnion([Q0]), "operationType" : NewBodyOperationType.ADD, "endBound" : BoundingType.UP_TO_SURFACE, "endBoundEntityFace" : qUnion([Q1]), "depth" : 25 * mm});
        }
    });
